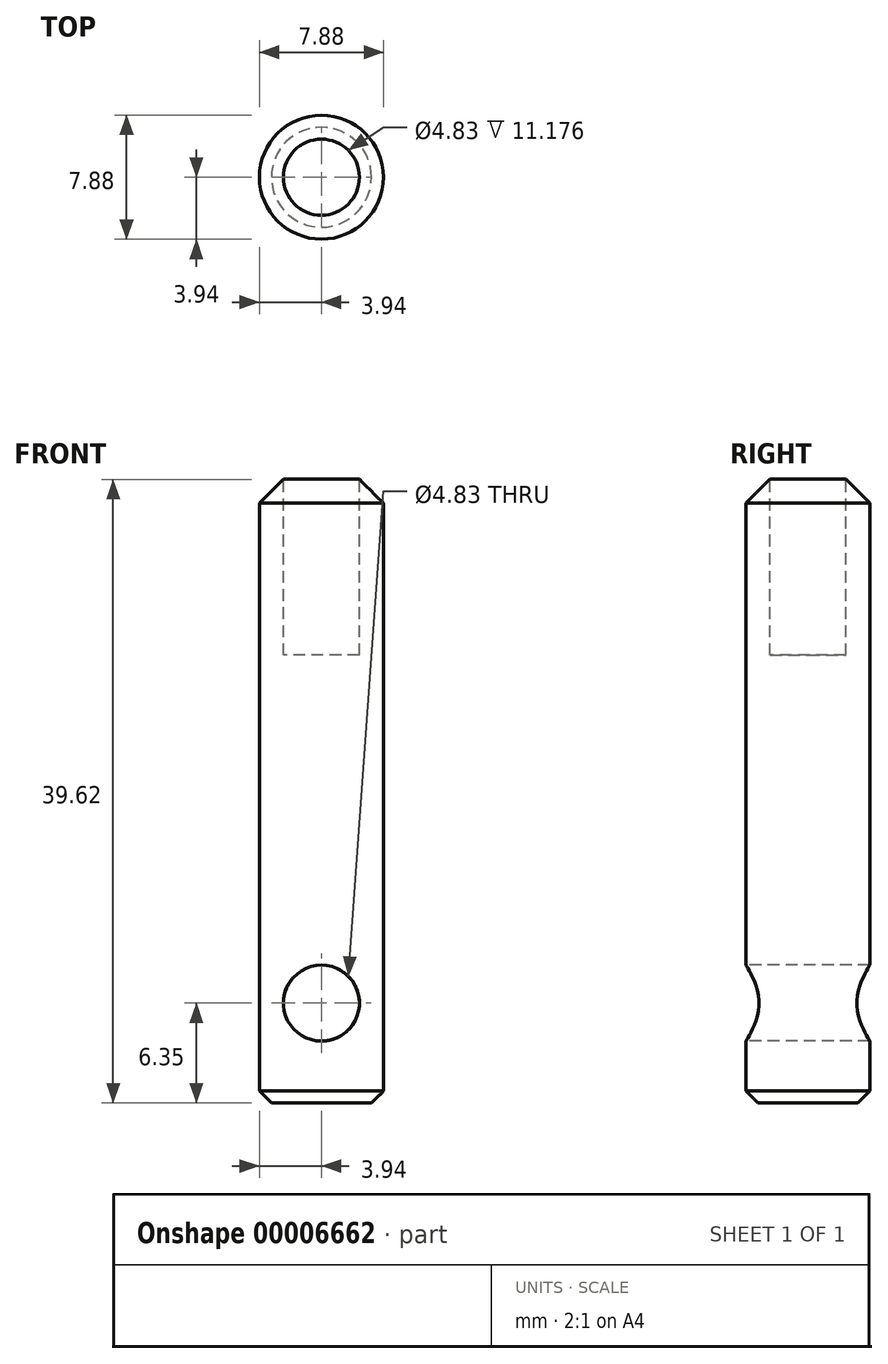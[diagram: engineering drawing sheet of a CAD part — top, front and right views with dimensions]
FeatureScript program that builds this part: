
annotation { "Feature Type Name" : "Feature", "Feature Type Description" : "" }
export const myFeature = defineFeature(function(context is Context, id is Id, definition is map)
    precondition{}
    {
        {
            var Q0;
            Q0=qCreatedBy(makeId("Top.planeOp"),FACE);
            var sketch = newSketch(context, id + "F0", { "sketchPlane" : qUnion([Q0])});
            skCircle(sketch, "E0", {"center": v(0, 0) * mm, "radius": 3.94 * mm});
            skSolve(sketch);
        }
        {
            var Q0;
            Q0 = qSketchRegion(id + "F0", true);
            extrude(context, id + "F1", {"entities" : qUnion([Q0]), "depth" : 39.62 * mm});
        }
        {
            var Q0;
            Q0=makeQuery(id+"F1.opExtrude","CAP_EDGE",EDGE,{"disambiguationData":[OSD([sQuery(id+"F0.wireOp",EDGE,"E0")])],"isStart":false});
            chamfer(context, id + "F2", {"entities" : qUnion([Q0]), "width" : 1.52 * mm, "tangentPropagation" : true});
        }
        {
            var Q0;
            Q0=makeQuery(id+"F1.opExtrude","CAP_EDGE",EDGE,{"disambiguationData":[OSD([sQuery(id+"F0.wireOp",EDGE,"E0")])],"isStart":true});
            chamfer(context, id + "F3", {"entities" : qUnion([Q0]), "width" : 0.76 * mm, "tangentPropagation" : true});
        }
        {
            var Q0;
            Q0=makeQuery(id+"F1.opExtrude","CAP_FACE",FACE,{"disambiguationData":[OSD([sQuery(id+"F0.wireOp",EDGE,"E0")])],"isStart":false});
            extrude(context, id + "F4", {"entities" : qUnion([Q0]), "operationType" : NewBodyOperationType.REMOVE, "oppositeDirection" : true, "depth" : 11.18 * mm});
        }
        {
            var Q0;
            Q0=qCreatedBy(makeId("Front.planeOp"),FACE);
            var sketch = newSketch(context, id + "F5", { "sketchPlane" : qUnion([Q0])});
            skLineSegment(sketch, "E1", {"start": v(0, 6.35) * mm, "end": v(0, -6.35) * mm});
            skLineSegment(sketch, "E2", {"start": v(0, -6.35) * mm, "end": v(12.14, -6.35) * mm});
            skLineSegment(sketch, "E3", {"start": v(12.14, -6.35) * mm, "end": v(12.14, 0) * mm});
            skCircle(sketch, "E4", {"center": v(0, 6.35) * mm, "radius": 2.41 * mm});
            skSolve(sketch);
        }
        {
            var Q0;
            Q0 = qSketchRegion(id + "F5", true);
            extrude(context, id + "F6", {"entities" : qUnion([Q0]), "operationType" : NewBodyOperationType.REMOVE, "oppositeDirection" : true, "depth" : 25.4 * mm});
        }
        {
            var Q0;
            Q0 = qSketchRegion(id + "F5", true);
            extrude(context, id + "F7", {"entities" : qUnion([Q0]), "operationType" : NewBodyOperationType.REMOVE, "depth" : 25.4 * mm});
        }
    });
